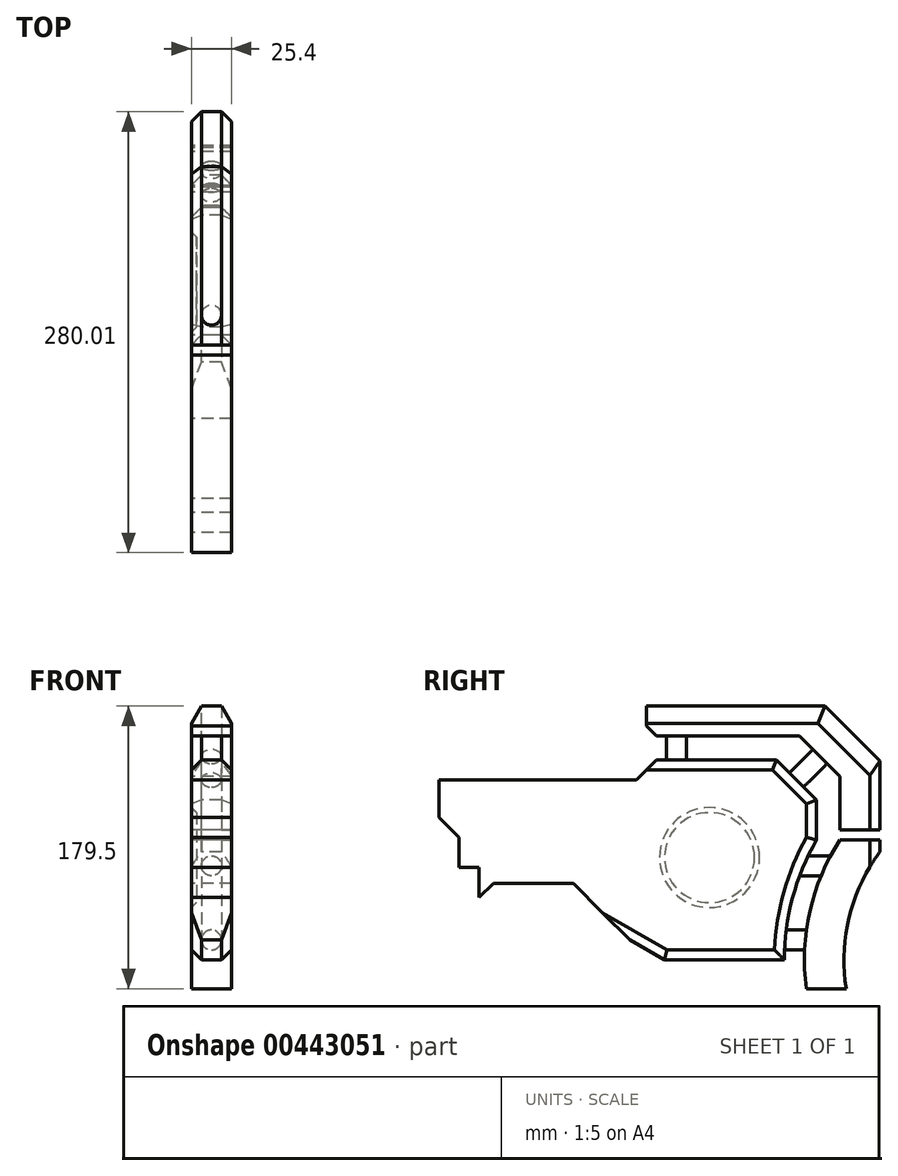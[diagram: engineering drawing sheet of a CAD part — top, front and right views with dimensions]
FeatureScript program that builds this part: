
annotation { "Feature Type Name" : "Feature", "Feature Type Description" : "" }
export const myFeature = defineFeature(function(context is Context, id is Id, definition is map)
    precondition{}
    {
        {
            var Q0;
            Q0=qCreatedBy(makeId("Right.planeOp"),FACE);
            var sketch = newSketch(context, id + "F0", { "sketchPlane" : qUnion([Q0])});
            skArc(sketch, "E0", {"start": v(-131.98, 76.2) * mm, "mid": v(-147.2, 39.44) * mm, "end": v(-152.4, 0) * mm});
            skLineSegment(sketch, "E1", {"start": v(-152.4, 0) * mm, "end": v(-228.6, 0) * mm});
            skLineSegment(sketch, "E2", {"start": v(-131.98, 76.2) * mm, "end": v(-131.98, 101.6) * mm});
            skLineSegment(sketch, "E3", {"start": v(0, 0) * mm, "end": v(-99.22, 57.28) * mm});
            skArc(sketch, "E4", {"start": v(-117.09, 76.2) * mm, "mid": v(-136.24, 30.9) * mm, "end": v(-138.5, -18.23) * mm});
            skLineSegment(sketch, "E5", {"start": v(-131.98, 101.6) * mm, "end": v(-157.38, 127) * mm});
            skLineSegment(sketch, "E6", {"start": v(-138.5, -18.23) * mm, "end": v(-113.1, -18.23) * mm});
            skLineSegment(sketch, "E7", {"start": v(0, 0) * mm, "end": v(-113.59, -14.95) * mm});
            skArc(sketch, "E8", {"start": v(-85.55, 76.2) * mm, "mid": v(-109.98, 32.1) * mm, "end": v(-113.1, -18.23) * mm});
            skLineSegment(sketch, "E9", {"start": v(-157.38, 127) * mm, "end": v(-233.58, 127) * mm});
            skLineSegment(sketch, "E10", {"start": v(-117.09, 76.2) * mm, "end": v(-85.55, 76.2) * mm});
            skLineSegment(sketch, "E11", {"start": v(-117.09, 76.2) * mm, "end": v(-117.09, 82.55) * mm});
            skLineSegment(sketch, "E12", {"start": v(-117.09, 82.55) * mm, "end": v(-91.69, 82.55) * mm});
            skLineSegment(sketch, "E13", {"start": v(-91.69, 82.55) * mm, "end": v(-91.69, 126.36) * mm});
            skLineSegment(sketch, "E14", {"start": v(-117.09, 82.55) * mm, "end": v(-117.09, 116.5) * mm});
            skLineSegment(sketch, "E15", {"start": v(-117.09, 116.5) * mm, "end": v(-142.81, 142.22) * mm});
            skLineSegment(sketch, "E16", {"start": v(-131.98, 101.6) * mm, "end": v(-117.09, 116.5) * mm});
            skLineSegment(sketch, "E17", {"start": v(-142.81, 142.22) * mm, "end": v(-233.58, 142.22) * mm});
            skLineSegment(sketch, "E18", {"start": v(-233.58, 142.22) * mm, "end": v(-239.93, 148.57) * mm});
            skLineSegment(sketch, "E19", {"start": v(-239.93, 148.57) * mm, "end": v(-239.93, 161.27) * mm});
            skLineSegment(sketch, "E20", {"start": v(-239.93, 161.27) * mm, "end": v(-126.6, 161.27) * mm});
            skLineSegment(sketch, "E21", {"start": v(-91.69, 126.36) * mm, "end": v(-126.6, 161.27) * mm});
            skLineSegment(sketch, "E22", {"start": v(-228.6, 0) * mm, "end": v(-250.6, 12.7) * mm});
            skLineSegment(sketch, "E23", {"start": v(-250.6, 12.7) * mm, "end": v(-286.52, 48.62) * mm});
            skLineSegment(sketch, "E24", {"start": v(-286.52, 48.62) * mm, "end": v(-337.32, 48.62) * mm});
            skLineSegment(sketch, "E25", {"start": v(-337.32, 48.62) * mm, "end": v(-346.3, 39.64) * mm});
            skLineSegment(sketch, "E26", {"start": v(-346.3, 39.64) * mm, "end": v(-346.3, 58.7) * mm});
            skLineSegment(sketch, "E27", {"start": v(-346.3, 58.7) * mm, "end": v(-359, 58.7) * mm});
            skLineSegment(sketch, "E28", {"start": v(-359, 58.7) * mm, "end": v(-359, 77.74) * mm});
            skLineSegment(sketch, "E29", {"start": v(-359, 77.74) * mm, "end": v(-371.7, 90.44) * mm});
            skLineSegment(sketch, "E30", {"start": v(-371.7, 90.44) * mm, "end": v(-371.7, 103.14) * mm});
            skLineSegment(sketch, "E31", {"start": v(-233.58, 127) * mm, "end": v(-246.28, 114.3) * mm});
            skLineSegment(sketch, "E32", {"start": v(-246.28, 114.3) * mm, "end": v(-371.7, 114.3) * mm});
            skLineSegment(sketch, "E33", {"start": v(-371.7, 114.3) * mm, "end": v(-371.7, 103.14) * mm});
            skLineSegment(sketch, "E34", {"start": v(-152.27, 6.35) * mm, "end": v(-139.56, 6.35) * mm});
            skLineSegment(sketch, "E35", {"start": v(-138.4, 19.05) * mm, "end": v(-151.2, 19.05) * mm});
            skLineSegment(sketch, "E36", {"start": v(-129.07, 53.46) * mm, "end": v(-142.72, 53.46) * mm});
            skLineSegment(sketch, "E37", {"start": v(-105.84, 43.84) * mm, "end": v(0, 0) * mm});
            skLineSegment(sketch, "E38", {"start": v(-123.04, 66.16) * mm, "end": v(-137.29, 66.16) * mm});
            skLineSegment(sketch, "E39", {"start": v(-227.23, 142.22) * mm, "end": v(-227.23, 127) * mm});
            skLineSegment(sketch, "E40", {"start": v(-214.53, 142.22) * mm, "end": v(-214.53, 127) * mm});
            skLineSegment(sketch, "E41", {"start": v(-144.68, 114.3) * mm, "end": v(-129.79, 129.2) * mm});
            skLineSegment(sketch, "E42", {"start": v(-149.17, 118.8) * mm, "end": v(-134.28, 133.68) * mm});
            skLineSegment(sketch, "E43", {"start": v(-125.3, 124.7) * mm, "end": v(-140.2, 109.8) * mm});
            skLineSegment(sketch, "E44", {"start": v(-85.55, 76.2) * mm, "end": v(-91.69, 76.2) * mm});
            skLineSegment(sketch, "E45", {"start": v(-91.69, 76.2) * mm, "end": v(-91.69, 68.7) * mm});
            skSolve(sketch);
        }
        {
            var Q0;
            {var subQ0=sQuery(id+"F0.wireOp",EDGE,"E41");Q0=makeQuery(id+"F0.imprint","IMPRINT",FACE,{"disambiguationData":[TD([[makeQuery(id+"F0.imprint","IMPRINT",EDGE,{"derivedFrom":subQ0}),1.0]])]});}
            var Q1;
            {var subQ0=sQuery(id+"F0.wireOp",EDGE,"E41");Q1=makeQuery(id+"F0.imprint","IMPRINT",FACE,{"disambiguationData":[TD([[makeQuery(id+"F0.imprint","IMPRINT",EDGE,{"derivedFrom":subQ0}),-1.0]])]});}
            var Q2;
            {var subQ0=sQuery(id+"F0.wireOp",EDGE,"E39");Q2=makeQuery(id+"F0.imprint","IMPRINT",FACE,{"disambiguationData":[TD([[makeQuery(id+"F0.imprint","IMPRINT",EDGE,{"derivedFrom":subQ0}),1.0]])]});}
            var Q3;
            {var subQ0=sQuery(id+"F0.wireOp",EDGE,"E36");Q3=makeQuery(id+"F0.imprint","IMPRINT",FACE,{"disambiguationData":[TD([[makeQuery(id+"F0.imprint","IMPRINT",EDGE,{"derivedFrom":subQ0}),-1.0]])]});}
            var Q4;
            {var subQ0=sQuery(id+"F0.wireOp",EDGE,"E34");Q4=makeQuery(id+"F0.imprint","IMPRINT",FACE,{"disambiguationData":[TD([[makeQuery(id+"F0.imprint","IMPRINT",EDGE,{"derivedFrom":subQ0}),1.0]])]});}
            extrude(context, id + "F1", {"entities" : qUnion([Q0, Q1, Q2, Q3, Q4]), "endBound" : BoundingType.SYMMETRIC, "depth" : 12.7 * mm});
        }
        {
            var Q0;
            {var subQ15=sQuery(id+"F0.wireOp",EDGE,"E1");Q0=makeQuery(id+"F0.imprint","IMPRINT",FACE,{"disambiguationData":[TD([[makeQuery(id+"F0.imprint","IMPRINT",EDGE,{"derivedFrom":subQ15}),-1.0]])]});}
            var Q1;
            Q1=makeQuery(id+"F0.imprint","IMPRINT",FACE,{"disambiguationData":[TD([[makeQuery(id+"F0.imprint","IMPRINT",EDGE,{"derivedFrom":sQuery(id+"F0.wireOp",EDGE,"E12")}),1.0]])]});
            var Q2;
            {var subQ0=sQuery(id+"F0.wireOp",EDGE,"E6");Q2=makeQuery(id+"F0.imprint","IMPRINT",FACE,{"disambiguationData":[TD([[makeQuery(id+"F0.imprint","IMPRINT",EDGE,{"derivedFrom":subQ0}),1.0]])]});}
            extrude(context, id + "F2", {"entities" : qUnion([Q0, Q1, Q2]), "endBound" : BoundingType.SYMMETRIC, "depth" : 25.4 * mm});
        }
        {
            var Q0;
            Q0=makeQuery(id+"F1.opExtrude","CAP_EDGE",EDGE,{"disambiguationData":[OSD([sQuery(id+"F0.wireOp",EDGE,"E42")])],"isStart":true});
            var Q1;
            Q1=makeQuery(id+"F1.opExtrude","CAP_EDGE",EDGE,{"disambiguationData":[OSD([sQuery(id+"F0.wireOp",EDGE,"E43")])],"isStart":true});
            var Q2;
            Q2=makeQuery(id+"F1.opExtrude","CAP_EDGE",EDGE,{"disambiguationData":[OSD([sQuery(id+"F0.wireOp",EDGE,"E43")])],"isStart":false});
            var Q3;
            Q3=makeQuery(id+"F1.opExtrude","CAP_EDGE",EDGE,{"disambiguationData":[OSD([sQuery(id+"F0.wireOp",EDGE,"E42")])],"isStart":false});
            var Q4;
            Q4=makeQuery(id+"F1.opExtrude","CAP_EDGE",EDGE,{"disambiguationData":[OSD([sQuery(id+"F0.wireOp",EDGE,"E38")])],"isStart":true});
            var Q5;
            Q5=makeQuery(id+"F1.opExtrude","CAP_EDGE",EDGE,{"disambiguationData":[OSD([sQuery(id+"F0.wireOp",EDGE,"E36")])],"isStart":true});
            var Q6;
            Q6=makeQuery(id+"F1.opExtrude","CAP_EDGE",EDGE,{"disambiguationData":[OSD([sQuery(id+"F0.wireOp",EDGE,"E38")])],"isStart":false});
            var Q7;
            Q7=makeQuery(id+"F1.opExtrude","CAP_EDGE",EDGE,{"disambiguationData":[OSD([sQuery(id+"F0.wireOp",EDGE,"E36")])],"isStart":false});
            var Q8;
            Q8=makeQuery(id+"F1.opExtrude","CAP_EDGE",EDGE,{"disambiguationData":[OSD([sQuery(id+"F0.wireOp",EDGE,"E35")])],"isStart":false});
            var Q9;
            Q9=makeQuery(id+"F1.opExtrude","CAP_EDGE",EDGE,{"disambiguationData":[OSD([sQuery(id+"F0.wireOp",EDGE,"E35")])],"isStart":true});
            var Q10;
            Q10=makeQuery(id+"F1.opExtrude","CAP_EDGE",EDGE,{"disambiguationData":[OSD([sQuery(id+"F0.wireOp",EDGE,"E34")])],"isStart":false});
            var Q11;
            Q11=makeQuery(id+"F1.opExtrude","CAP_EDGE",EDGE,{"disambiguationData":[OSD([sQuery(id+"F0.wireOp",EDGE,"E34")])],"isStart":true});
            var Q12;
            Q12=makeQuery(id+"F1.opExtrude","CAP_EDGE",EDGE,{"disambiguationData":[OSD([sQuery(id+"F0.wireOp",EDGE,"E39")])],"isStart":true});
            var Q13;
            Q13=makeQuery(id+"F1.opExtrude","CAP_EDGE",EDGE,{"disambiguationData":[OSD([sQuery(id+"F0.wireOp",EDGE,"E39")])],"isStart":false});
            var Q14;
            Q14=makeQuery(id+"F1.opExtrude","CAP_EDGE",EDGE,{"disambiguationData":[OSD([sQuery(id+"F0.wireOp",EDGE,"E40")])],"isStart":true});
            var Q15;
            Q15=makeQuery(id+"F1.opExtrude","CAP_EDGE",EDGE,{"disambiguationData":[OSD([sQuery(id+"F0.wireOp",EDGE,"E40")])],"isStart":false});
            fillet(context, id + "F3", {"entities" : qUnion([Q0, Q1, Q2, Q3, Q4, Q5, Q6, Q7, Q8, Q9, Q10, Q11, Q12, Q13, Q14, Q15]), "radius" : 6.35 * mm, "tangentPropagation" : true, "allowEdgeOverflow" : false});
        }
        {
            var Q0;
            Q0=makeQuery(id+"F2.opExtrude","CAP_EDGE",EDGE,{"disambiguationData":[OSD([sQuery(id+"F0.wireOp",EDGE,"E20")])],"isStart":false});
            var Q1;
            Q1=makeQuery(id+"F2.opExtrude","CAP_EDGE",EDGE,{"disambiguationData":[OSD([sQuery(id+"F0.wireOp",EDGE,"E20")])],"isStart":true});
            var Q2;
            Q2=makeQuery(id+"F2.opExtrude","CAP_EDGE",EDGE,{"disambiguationData":[OSD([sQuery(id+"F0.wireOp",EDGE,"E21")])],"isStart":true});
            var Q3;
            Q3=makeQuery(id+"F2.opExtrude","CAP_EDGE",EDGE,{"disambiguationData":[OSD([sQuery(id+"F0.wireOp",EDGE,"E21")])],"isStart":false});
            chamfer(context, id + "F4", {"entities" : qUnion([Q0, Q1, Q2, Q3]), "chamferType" : ChamferType.OFFSET_ANGLE, "width" : 6.35 * mm, "oppositeDirection" : false, "angle" : 60 * degree, "tangentPropagation" : true});
        }
        {
            var Q0;
            Q0=makeQuery(id+"F2.opExtrude","CAP_EDGE",EDGE,{"disambiguationData":[OSD([sQuery(id+"F0.wireOp",EDGE,"E13")])],"isStart":false});
            var Q1;
            Q1=makeQuery(id+"F2.opExtrude","CAP_EDGE",EDGE,{"disambiguationData":[OSD([sQuery(id+"F0.wireOp",EDGE,"E13")])],"isStart":true});
            var Q2;
            Q2=makeQuery(id+"F2.opExtrude","CAP_EDGE",EDGE,{"disambiguationData":[OSD([sQuery(id+"F0.wireOp",EDGE,"E9")])],"isStart":false});
            var Q3;
            Q3=makeQuery(id+"F2.opExtrude","CAP_EDGE",EDGE,{"disambiguationData":[OSD([sQuery(id+"F0.wireOp",EDGE,"E5")])],"isStart":false});
            var Q4;
            Q4=makeQuery(id+"F2.opExtrude","CAP_EDGE",EDGE,{"disambiguationData":[OSD([sQuery(id+"F0.wireOp",EDGE,"E2")])],"isStart":false});
            var Q5;
            Q5=makeQuery(id+"F2.opExtrude","CAP_EDGE",EDGE,{"disambiguationData":[OSD([sQuery(id+"F0.wireOp",EDGE,"E0")])],"isStart":false});
            var Q6;
            Q6=makeQuery(id+"F2.opExtrude","CAP_EDGE",EDGE,{"disambiguationData":[OSD([sQuery(id+"F0.wireOp",EDGE,"E9")])],"isStart":true});
            var Q7;
            Q7=makeQuery(id+"F2.opExtrude","CAP_EDGE",EDGE,{"disambiguationData":[OSD([sQuery(id+"F0.wireOp",EDGE,"E5")])],"isStart":true});
            var Q8;
            Q8=makeQuery(id+"F2.opExtrude","CAP_EDGE",EDGE,{"disambiguationData":[OSD([sQuery(id+"F0.wireOp",EDGE,"E2")])],"isStart":true});
            var Q9;
            Q9=makeQuery(id+"F2.opExtrude","CAP_EDGE",EDGE,{"disambiguationData":[OSD([sQuery(id+"F0.wireOp",EDGE,"E0")])],"isStart":true});
            var Q10;
            Q10=makeQuery(id+"F2.opExtrude","CAP_EDGE",EDGE,{"disambiguationData":[OSD([sQuery(id+"F0.wireOp",EDGE,"E45")])],"isStart":true});
            var Q11;
            Q11=makeQuery(id+"F2.opExtrude","CAP_EDGE",EDGE,{"disambiguationData":[OSD([sQuery(id+"F0.wireOp",EDGE,"E45")])],"isStart":false});
            var Q12;
            Q12=makeQuery(id+"F2.opExtrude","CAP_EDGE",EDGE,{"disambiguationData":[OSD([sQuery(id+"F0.wireOp",EDGE,"E1")])],"isStart":true});
            var Q13;
            Q13=makeQuery(id+"F2.opExtrude","CAP_EDGE",EDGE,{"disambiguationData":[OSD([sQuery(id+"F0.wireOp",EDGE,"E1")])],"isStart":false});
            var Q14;
            Q14=makeQuery(id+"F2.opExtrude","CAP_EDGE",EDGE,{"disambiguationData":[OSD([sQuery(id+"F0.wireOp",EDGE,"E22")])],"isStart":false});
            var Q15;
            Q15=makeQuery(id+"F2.opExtrude","CAP_EDGE",EDGE,{"disambiguationData":[OSD([sQuery(id+"F0.wireOp",EDGE,"E22")])],"isStart":true});
            chamfer(context, id + "F5", {"entities" : qUnion([Q0, Q1, Q2, Q3, Q4, Q5, Q6, Q7, Q8, Q9, Q10, Q11, Q12, Q13, Q14, Q15]), "width" : 6.35 * mm, "tangentPropagation" : true});
        }
        {
            var Q0;
            Q0=makeQuery(id+"F2.opExtrude","CAP_FACE",FACE,{"disambiguationData":[OSD([sQuery(id+"F0.wireOp",EDGE,"E0"),sQuery(id+"F0.wireOp",EDGE,"E1"),sQuery(id+"F0.wireOp",EDGE,"E2"),sQuery(id+"F0.wireOp",EDGE,"E5"),sQuery(id+"F0.wireOp",EDGE,"E9"),sQuery(id+"F0.wireOp",EDGE,"E22"),sQuery(id+"F0.wireOp",EDGE,"E23"),sQuery(id+"F0.wireOp",EDGE,"E24"),sQuery(id+"F0.wireOp",EDGE,"E25"),sQuery(id+"F0.wireOp",EDGE,"E26"),sQuery(id+"F0.wireOp",EDGE,"E27"),sQuery(id+"F0.wireOp",EDGE,"E28"),sQuery(id+"F0.wireOp",EDGE,"E29"),sQuery(id+"F0.wireOp",EDGE,"E30"),sQuery(id+"F0.wireOp",EDGE,"E31"),sQuery(id+"F0.wireOp",EDGE,"E32"),sQuery(id+"F0.wireOp",EDGE,"E33")])],"isStart":true});
            var sketch = newSketch(context, id + "F6", { "sketchPlane" : qUnion([Q0])});
            skPoint(sketch, "E46.0", {"position": v(233.58, 127) * mm});
            skPoint(sketch, "E47.0", {"position": v(199.97, 120.65) * mm});
            skLineSegment(sketch, "E48.0", {"start": v(246.28, 114.3) * mm, "end": v(371.7, 114.3) * mm});
            skLineSegment(sketch, "E49.0", {"start": v(286.52, 48.62) * mm, "end": v(337.32, 48.62) * mm});
            skLineSegment(sketch, "E50", {"start": v(297.83, 114.3) * mm, "end": v(297.83, 48.62) * mm});
            skLineSegment(sketch, "E51", {"start": v(297.83, 81.46) * mm, "end": v(297.83, 48.62) * mm});
            skCircle(sketch, "E52", {"center": v(199.97, 65.04) * mm, "radius": 31.75 * mm});
            skPoint(sketch, "E52.centerSnap0", {"position": v(297.83, 65.04) * mm});
            skSolve(sketch);
        }
        {
            var Q0;
            Q0=makeQuery(id+"F6.imprint","IMPRINT",FACE,{"disambiguationData":[TD([[makeQuery(id+"F6.imprint","IMPRINT",EDGE,{"derivedFrom":sQuery(id+"F6.wireOp",EDGE,"E52")}),1.0]])]});
            extrude(context, id + "F7", {"entities" : qUnion([Q0]), "operationType" : NewBodyOperationType.REMOVE, "oppositeDirection" : true, "depth" : 3.17 * mm});
        }
        {
            var Q0;
            Q0=makeQuery(id+"F7.boolean.opBoolean","COPY",EDGE,{"derivedFrom":makeQuery(id+"F7.opExtrude","CAP_EDGE",EDGE,{"disambiguationData":[OSD([sQuery(id+"F6.wireOp",EDGE,"E52")])],"isStart":false})});
            chamfer(context, id + "F8", {"entities" : qUnion([Q0]), "width" : 3.17 * mm, "tangentPropagation" : true});
        }
    });
